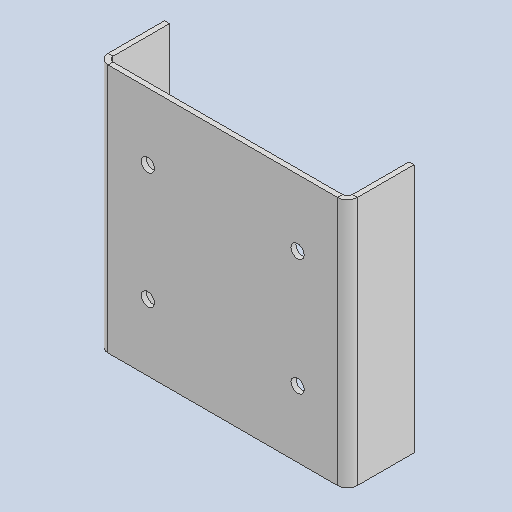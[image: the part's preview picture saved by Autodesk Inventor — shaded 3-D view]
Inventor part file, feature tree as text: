
AUTODESK INVENTOR PART (.ipt)
format: ipt  version: 2025 (Build 290162010, 162A)  size: 224,256 bytes
history: native  units: mm
features: sheet_metal_op x4, other x3, extrude x2, pattern_circular x1, projected_geometry x1, sketch x1
ambient origin geometry x8: Origin, YZ Plane, XZ Plane, XY Plane, X Axis, Y Axis, Z Axis, Center Point
bodies: Solid1 (feature_tree)
feature tree (12):
  sheet_metal_op  "Face1"
  extrude  "Extrusion1"  Depth=150.0mm
  sheet_metal_op  "Flange1"
  extrude  "Extrusion2"  Depth=150.0mm
  pattern_circular  "Circular Pattern1"  [2 undecoded]
  other  "Plate1"
  projected_geometry  "Projected Loop1"
  sketch  "Sketch3"  dims[d0=3.0mm d1=150.0mm d2=150.0mm d3=35.0mm d4=90.0mm d5=70.0mm d7=8.0mm d8=0.0mm d9=0.0mm d10=3.0mm d11=1.5mm d12=6.0mm d13=3.0mm d14=40.0mm d15=90.0deg d16=3.0mm d17=12.0mm d18=3.0mm d19=3.0mm d20=20.0mm d21=6.0mm d22=30.0mm d23=60.0deg d24=30.0deg d25=6.0mm d26=40.0mm d27=0.0mm d28=0.0mm d29=40.0mm d30=360.0deg]
  other  "Plate2"
  sheet_metal_op  "Bend1"
  sheet_metal_op  "Corner1"
  other  "Definition1"
note: 2 required parameter values undecoded (feature->parameter linkage not recoverable at this tier; creation-order binding heuristic only, values carry confidence <= 0.55)
